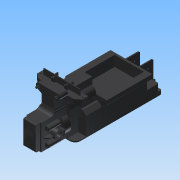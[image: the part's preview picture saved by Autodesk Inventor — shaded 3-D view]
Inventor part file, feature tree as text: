
AUTODESK INVENTOR PART (.ipt)
format: ipt  version: 2014 (Build 180170000, 170)  size: 742,400 bytes
history: native  units: in
note: dims shown in document units (in); Inventor stores cm internally (conversion verified against a paired STEP export)
features: extrude x28, sketch x28, projected_geometry x8, fillet x5, mirror x4, chamfer x1, plane x1, other x1
ambient origin geometry x8: Origin, YZ Plane, XZ Plane, XY Plane, X Axis, Y Axis, Z Axis, Center Point
bodies: Solid1 (feature_tree)
feature tree (76):
  extrude  "Extrusion1"  Depth=0.11in
  extrude  "Extrusion2"  Depth=1.25in
  mirror  "Mirror1"
  fillet  "Fillet1"  Radius=1.25in
  extrude  "Extrusion3"  Depth=0.3in
  extrude  "Extrusion4"  Depth=1.18in TaperAngle=0.0deg
  extrude  "Extrusion5"  Depth=0.125in
  chamfer  "Chamfer1"  Distance=0.546in
  extrude  "Extrusion6"  Depth=0.55in TaperAngle=0.0deg
  plane  "Work Plane1"
  mirror  "Mirror2"
  mirror  "Mirror3"
  extrude  "Extrusion7"  Depth=1.14in
  fillet  "Fillet2"  Radius=1.14in
  fillet  "Fillet3"  Radius=0.355in
  extrude  "Extrusion8"  Depth=0.11in
  extrude  "Extrusion9"  Depth=0.6in
  extrude  "Extrusion10"  Depth=0.125in TaperAngle=45.0deg
  extrude  "Extrusion11"  Depth=0.4in TaperAngle=0.0deg
  extrude  "Extrusion12"  Depth=0.38in
  mirror  "Mirror4"
  extrude  "Extrusion13"  Depth=2.56in
  extrude  "Extrusion14"  Depth=1.96in
  extrude  "Extrusion15"  Depth=1.17in
  extrude  "Extrusion16"  Depth=0.125in
  extrude  "Extrusion17"  Depth=0.125in
  extrude  "Extrusion18"  Depth=0.91in
  extrude  "Extrusion19"  Depth=0.3in
  extrude  "Extrusion20"  Depth=0.17in
  extrude  "Extrusion21"  Depth=0.125in
  extrude  "Extrusion22"  Depth=0.2in
  extrude  "Extrusion23"  Depth=1.58in
  extrude  "Extrusion24"  Depth=1.0in
  extrude  "Extrusion25"  Depth=1.58in
  fillet  "Fillet4"  Radius=0.125in
  fillet  "Fillet5"  Radius=0.37in
  extrude  "Extrusion26"  Depth=1.0in
  extrude  "Extrusion27"  Depth=1.0in
  extrude  "Extrusion28"  Depth=1.0in TaperAngle=0.0deg
  sketch  "Sketch1"  dims[d13=2.45in d15=0.11in]
  sketch  "Sketch2"  dims[d16=0.44in d17=2.33in d18=1.25in]
  sketch  "Sketch3"  dims[d19=1.11in d20=0.3in]
  sketch  "Sketch4"  dims[d21=2.74in d22=1.18in d23=0.0in]
  sketch  "Sketch5"  dims[d24=0.1in d25=0.0in d26=0.125in]
  projected_geometry  "Projected Loop1"
  sketch  "Sketch6"  dims[d27=0.82in]
  other  "Work Axis1"
  sketch  "Sketch7"  dims[d28=0.736in]
  sketch  "Sketch9"  dims[d29=0.85in]
  sketch  "Sketch10"  dims[d30=0.48in d31=0.546in d32=0.0in]
  sketch  "Sketch11"  dims[d33=0.337in d37=0.55in d38=0.0in]
  sketch  "Sketch12"  dims[d39=1.146in d40=0.43in d41=1.14in d42=0.355in]
  sketch  "Sketch13"  dims[d43=0.384in d44=0.11in]
  sketch  "Sketch14"  dims[d45=0.08in d46=0.6in]
  sketch  "Sketch15"  dims[d47=0.4in d48=0.0in d49=0.25in d50=0.125in d51=45.0deg]
  sketch  "Sketch16"  dims[d52=0.125in d54=0.4in d55=0.0in]
  sketch  "Sketch17"  dims[d56=90.0deg d57=0.38in]
  sketch  "Sketch18"  dims[d58=2.56in d59=0.64in]
  sketch  "Sketch19"  dims[d60=1.96in d61=0.15in]
  sketch  "Sketch20"  dims[d62=1.7098in d63=1.17in]
  sketch  "Sketch21"  dims[d64=1.18in d65=0.0in d66=0.125in]
  sketch  "Sketch22"  dims[d67=0.125in d69=0.49in]
  sketch  "Sketch23"  dims[d70=0.77in d71=0.0in d72=0.91in]
  projected_geometry  "Projected Loop2"
  sketch  "Sketch24"  dims[d73=0.274in d74=0.3in]
  projected_geometry  "Projected Loop3"
  projected_geometry  "Projected Loop4"
  sketch  "Sketch25"  dims[d75=0.17in d76=0.57in]
  projected_geometry  "Projected Loop5"
  projected_geometry  "Projected Loop6"
  projected_geometry  "Projected Loop7"
  projected_geometry  "Projected Loop8"
  sketch  "Sketch26"  dims[d77=0.42in d78=0.125in]
  sketch  "Sketch27"  dims[d79=0.77in d80=0.0in d81=0.2in]
  sketch  "Sketch28"  dims[d83=0.1in d84=1.58in]
  sketch  "Sketch29"  dims[d85=0.24in d86=0.0in d87=1.15in d88=1.58in d89=0.125in d90=0.37in d91=0.18in d92=0.586in d93=0.51in d94=0.0in d95=0.08in d96=0.47in d97=0.0in d100=0.3in d101=1.0in d103=1.4in d104=0.47in d105=0.0in d106=0.07in d110=0.538in d111=0.0in d112=3.53in d114=0.31in d115=0.07in d116=0.07in d118=0.23in d119=0.1in d120=1.18in d121=0.127in d122=0.47in d123=0.0in d124=0.2in d125=45.0deg d126=0.52in d127=0.13in d128=1.5in d129=0.0in d131=0.1in d132=1.5in d133=0.0in d134=0.75in d136=2.15in d137=0.5in d138=0.47in d139=4.37in d140=0.0in d141=0.375in d142=0.0in d143=1.129in d144=1.4in d145=0.67in d146=0.0in d147=0.1in d148=1.42in d149=1.19in d150=1.47in d151=0.0in d152=1.47in d153=0.0in d154=0.44in d155=0.135in d156=0.0in d157=0.21in d158=0.6in d159=0.0in d160=0.135in d161=0.0in d162=0.5in d163=0.125in d164=0.125in d165=0.167in d166=0.56in d167=1.98in d168=0.15in d169=0.89in d171=0.17in d172=0.135in d173=0.0in d174=1.95in d175=5.68in d176=0.75in d177=0.0in d178=2.82in d179=3.96in d180=1.0in d181=0.0in]
